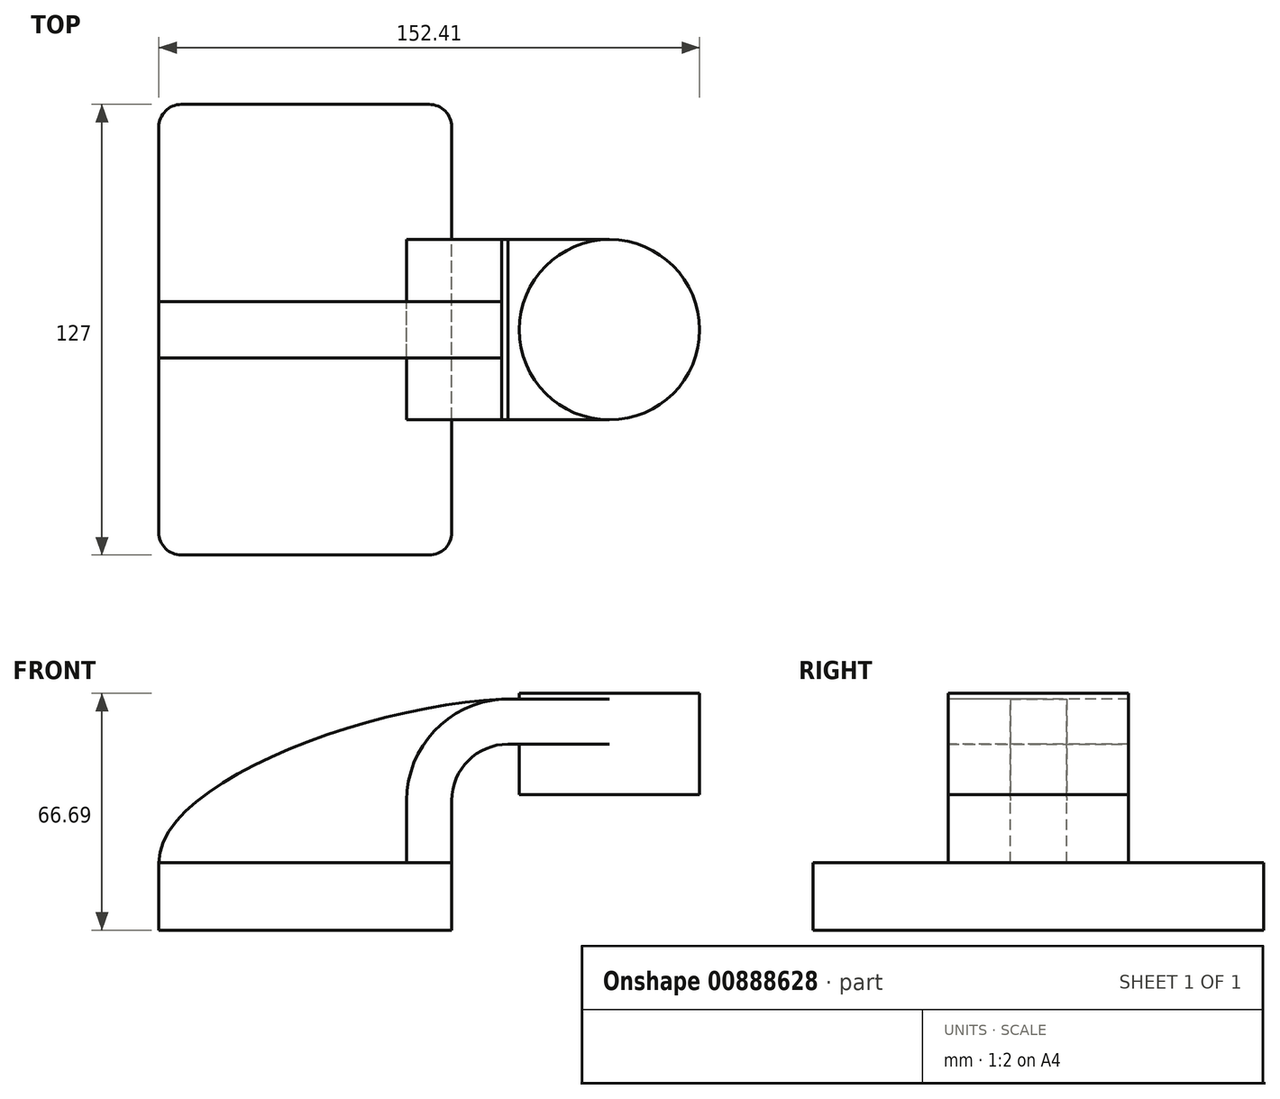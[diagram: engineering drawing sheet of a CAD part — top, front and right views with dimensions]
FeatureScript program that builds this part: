
annotation { "Feature Type Name" : "Feature", "Feature Type Description" : "" }
export const myFeature = defineFeature(function(context is Context, id is Id, definition is map)
    precondition{}
    {
        {
            var Q0;
            Q0=qCreatedBy(makeId("Front.planeOp"),FACE);
            var sketch = newSketch(context, id + "F0", { "sketchPlane" : qUnion([Q0])});
            skLineSegment(sketch, "E0.bottom", {"start": v(-41.28, 9.52) * mm, "end": v(41.27, 9.53) * mm});
            skLineSegment(sketch, "E0.top", {"start": v(-41.28, -9.53) * mm, "end": v(41.28, -9.53) * mm});
            skLineSegment(sketch, "E0.left", {"start": v(-41.28, 9.52) * mm, "end": v(-41.27, -9.53) * mm});
            skLineSegment(sketch, "E0.right", {"start": v(41.28, 9.53) * mm, "end": v(41.28, -9.52) * mm});
            skPoint(sketch, "E0.middle", {"position": v(0, 0) * mm});
            skLineSegment(sketch, "E1.bottom", {"start": v(60.32, 57.16) * mm, "end": v(111.12, 57.16) * mm});
            skLineSegment(sketch, "E1.top", {"start": v(60.32, 28.59) * mm, "end": v(111.12, 28.59) * mm});
            skLineSegment(sketch, "E1.left", {"start": v(60.32, 57.16) * mm, "end": v(60.32, 28.59) * mm});
            skLineSegment(sketch, "E1.right", {"start": v(111.12, 57.16) * mm, "end": v(111.12, 28.59) * mm});
            skPoint(sketch, "E1.middle", {"position": v(85.72, 42.88) * mm});
            skLineSegment(sketch, "E2", {"start": v(41.27, 9.53) * mm, "end": v(41.27, 27) * mm});
            skArc(sketch, "E3", {"start": v(41.27, 27) * mm, "mid": v(45.92, 38.23) * mm, "end": v(57.15, 42.88) * mm});
            skPoint(sketch, "E3.endSnap0", {"position": v(60.32, 42.88) * mm});
            skLineSegment(sketch, "E4", {"start": v(57.15, 42.88) * mm, "end": v(85.72, 42.88) * mm});
            skLineSegment(sketch, "E5.0", {"start": v(57.15, 55.58) * mm, "end": v(85.72, 55.58) * mm});
            skArc(sketch, "E5.1", {"start": v(28.57, 27) * mm, "mid": v(36.94, 47.2) * mm, "end": v(57.15, 55.58) * mm});
            skLineSegment(sketch, "E5.2", {"start": v(28.57, 9.53) * mm, "end": v(28.57, 27) * mm});
            skLineSegment(sketch, "E6", {"start": v(85.72, 28.59) * mm, "end": v(85.72, 57.16) * mm});
            skFitSpline(sketch, "E7", {"points": [v(-41.28, 9.53) * mm, v(57.15, 55.58) * mm], "startDerivative": vector(-0.21, 68.55) * mm, "endDerivative": vector(113.04, 2.66) * mm});
            skSolve(sketch);
        }
        {
            var Q0;
            Q0=makeQuery(id+"F0.imprint","IMPRINT",FACE,{"disambiguationData":[TD([[makeQuery(id+"F0.imprint","IMPRINT",EDGE,{"derivedFrom":sQuery(id+"F0.wireOp",EDGE,"E0.top")}),1.0]])]});
            extrude(context, id + "F1", {"entities" : qUnion([Q0]), "endBound" : BoundingType.SYMMETRIC, "depth" : 127 * mm, "offsetDistance" : 25.4 * mm});
        }
        {
            var Q0;
            {var subQ1=sQuery(id+"F0.wireOp",EDGE,"E2");Q0=makeQuery(id+"F0.imprint","IMPRINT",FACE,{"disambiguationData":[TD([[makeQuery(id+"F0.imprint","IMPRINT",EDGE,{"derivedFrom":subQ1}),1.0]])]});}
            var Q1;
            {var subQ0=sQuery(id+"F0.wireOp",EDGE,"E5.0");var subQ1=sQuery(id+"F0.wireOp",EDGE,"E1.left");var subQ2=makeQuery(id+"F0.imprint","INTERSECT",VERTEX,{"derivedFrom":[subQ1,subQ0]});Q1=makeQuery(id+"F0.imprint","IMPRINT",FACE,{"disambiguationData":[TD([[makeQuery(id+"F0.imprint","IMPRINT",EDGE,{"disambiguationData":[TD([[subQ2,-1.0]])],"derivedFrom":subQ1}),1.0]])]});}
            extrude(context, id + "F2", {"entities" : qUnion([Q0, Q1]), "endBound" : BoundingType.SYMMETRIC, "depth" : 50.8 * mm, "offsetDistance" : 25.4 * mm});
        }
        {
            var Q0;
            {var subQ3=sQuery(id+"F0.wireOp",EDGE,"E5.2");Q0=makeQuery(id+"F0.imprint","IMPRINT",FACE,{"disambiguationData":[TD([[makeQuery(id+"F0.imprint","IMPRINT",EDGE,{"derivedFrom":subQ3}),1.0]])]});}
            extrude(context, id + "F3", {"entities" : qUnion([Q0]), "endBound" : BoundingType.SYMMETRIC, "depth" : 15.88 * mm, "offsetDistance" : 25.4 * mm});
        }
        {
            var Q0;
            {var subQ4=sQuery(id+"F0.wireOp",EDGE,"E1.right");Q0=makeQuery(id+"F0.imprint","IMPRINT",FACE,{"disambiguationData":[TD([[makeQuery(id+"F0.imprint","IMPRINT",EDGE,{"derivedFrom":subQ4}),-1.0]])]});}
            var Q1;
            Q1=sQuery(id+"F0.wireOp",EDGE,"E6");
            revolve(context, id + "F4", {"operationType" : NewBodyOperationType.ADD, "surfaceOperationType" : NewSurfaceOperationType.NEW, "entities" : qUnion([Q0]), "axis" : qUnion([Q1]), "revolveType" : RevolveType.FULL});
        }
        {
            var Q0;
            Q0=makeQuery(id+"F1.opExtrude","CAP_EDGE",EDGE,{"disambiguationData":[OSD([sQuery(id+"F0.wireOp",EDGE,"E0.right")])],"isStart":false});
            var Q1;
            Q1=makeQuery(id+"F1.opExtrude","CAP_EDGE",EDGE,{"disambiguationData":[OSD([sQuery(id+"F0.wireOp",EDGE,"E0.right")])],"isStart":true});
            var Q2;
            Q2=makeQuery(id+"F1.opExtrude","CAP_EDGE",EDGE,{"disambiguationData":[OSD([sQuery(id+"F0.wireOp",EDGE,"E0.left")])],"isStart":false});
            var Q3;
            Q3=makeQuery(id+"F1.opExtrude","CAP_EDGE",EDGE,{"disambiguationData":[OSD([sQuery(id+"F0.wireOp",EDGE,"E0.left")])],"isStart":true});
            fillet(context, id + "F5", {"entities" : qUnion([Q0, Q1, Q2, Q3]), "radius" : 6.35 * mm, "tangentPropagation" : true, "allowEdgeOverflow" : false});
        }
    });
